# Revit family: Work_Tools_&_Leg_Screens-Teknion-CQCTB_Routes_Tech_Board-R2022
name_source: partatom
category: Furniture
units: mm (PartAtom-declared; Revit-internal decimal feet)

## family parameters
Always vertical = Yes
Cut with Voids When Loaded = No
OmniClass Number = 23.40.20.00
OmniClass Title = General Furniture and Specialties
Render Appearance Source = Family Geometry
Room Calculation Point = No
Shared = Yes
Work Plane-Based = No

## types (4) — shared parameters
Assembly Code = E2020200
Manufacturer = Teknion
Manufacturer Fax = 416.661.4586
Part Number = CQCTB
Product Documentation Link = https://assets.teknion.com
Product Line = Routes
Product Page URL = https://www.teknion.com
Series = Routes
Sustainability Data = https://www.teknion.com
URL = www.teknion.com
Unit Weight URL = http://www.teknion.com
Warranty = http://www.teknion.com
zero-valued in all types: Default Elevation

## per-type parameters (varying)
| type | 2D Add On Board | Description | Left Tackboard Add On | Left Whiteboard Add On | Model | Right Tackboard Add On Board | Right Whiteboard Add On Board |
| One Whiteboard Add Ons & One Tackboard Add Ons, 77" h x 64" w | Yes | Routes Tech Board, One Whiteboard Add Ons & One Tackboard Add Ons, 77" Height, 64" Width, Vesa Screen Mount up to 65" | No | Yes | CQCTBU7764S | Yes | No |
| No Add Ons, 77" h x 64" w | No | Routes Tech Board, No Add Ons, 77" Height, 64" Width, Vesa Screen Mount up to 65" | No | No | CQCTBN7764S | No | No |
| Two Tackboard Add Ons, 77" h x 64" w | Yes | Routes Tech Board, Two Tackboard Add Ons, 77" Height, 64" Width, Vesa Screen Mount up to 65" | Yes | No | CQCTBT7764S | Yes | No |
| Two Whiteboard Add Ons, 77" h x 64" w | Yes | Routes Tech Board, Two Whiteboard Add Ons, 77" Height, 64" Width, Vesa Screen Mount up to 65" | No | Yes | CQCTBW7764S | No | Yes |

## geometry (parser evidence)
native form markers: Sweep x4
no freeform markers — native parametric forms only
